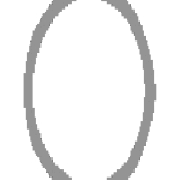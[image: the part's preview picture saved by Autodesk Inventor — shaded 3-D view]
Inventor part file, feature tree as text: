
AUTODESK INVENTOR PART (.ipt)
format: ipt  version: 2021 (Build 250183000, 183)  size: 112,128 bytes
history: native  units: in
note: dims shown in document units (in); Inventor stores cm internally (conversion verified against a paired STEP export)
features: other x4, sketch x3, plane x1
ambient origin geometry x8: Origin, YZ Plane, XZ Plane, XY Plane, X Axis, Y Axis, Z Axis, Center Point
bodies: Solid1 (feature_tree), Body (feature_tree)
feature tree (8):
  other  "Driven Length"
  other  "Frame Generator"
  other  "Start Plane"
  other  "End Plane"
  sketch  "Sketch"  dims[d2=29.4in d4=-0.0in d5=29.4in d6=0.12in d7=0.0in d8=90.0deg d9=29.4in]
  sketch  "Sketch2"  dims[d0=1.0in]
  plane  "Work Plane3"
  sketch  "Sketch3"  dims[d1=0.065in]
